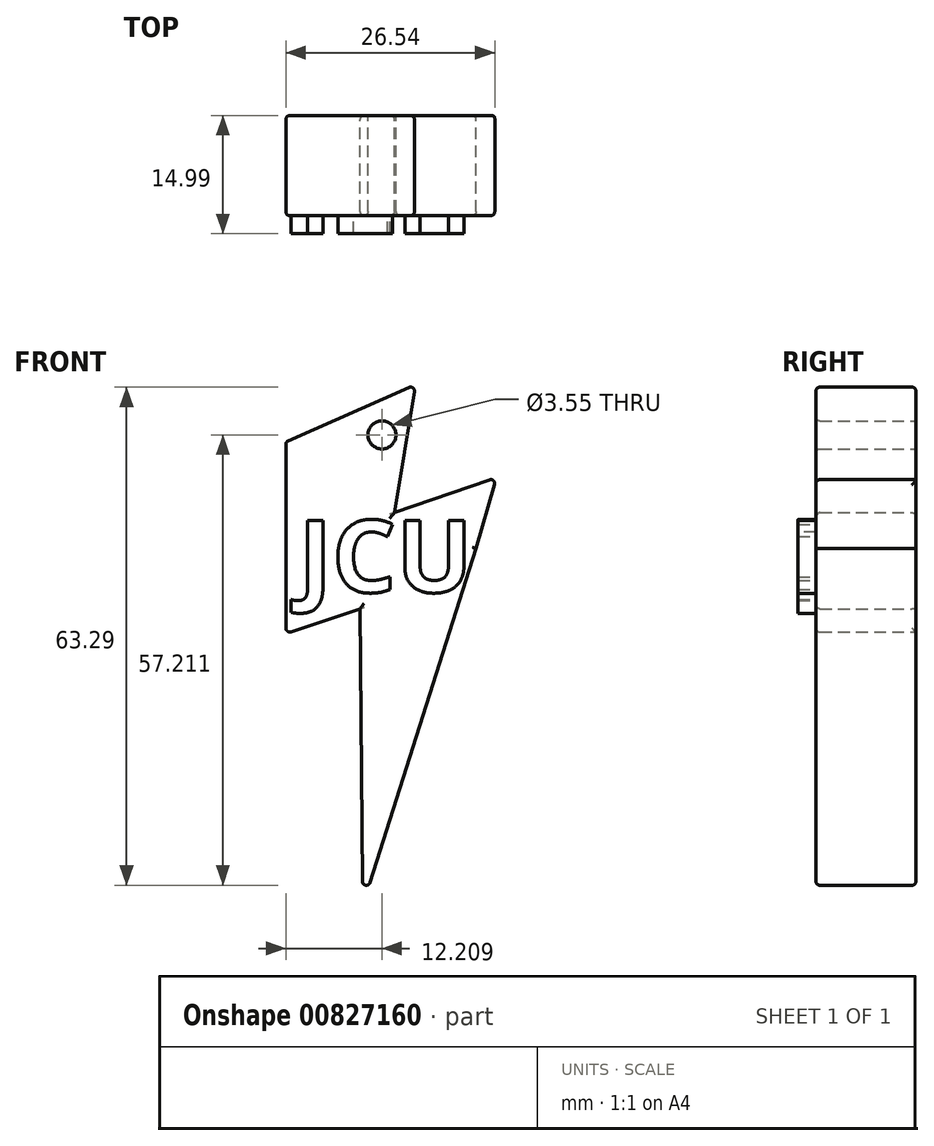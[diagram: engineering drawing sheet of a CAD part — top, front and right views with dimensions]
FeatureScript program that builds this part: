
annotation { "Feature Type Name" : "Feature", "Feature Type Description" : "" }
export const myFeature = defineFeature(function(context is Context, id is Id, definition is map)
    precondition{}
    {
        {
            var Q0;
            Q0=qCreatedBy(makeId("Front.planeOp"),FACE);
            var sketch = newSketch(context, id + "F0", { "sketchPlane" : qUnion([Q0])});
            skLineSegment(sketch, "E0", {"start": v(-13.8, 13.56) * mm, "end": v(-13.8, -10.8) * mm});
            skLineSegment(sketch, "E1", {"start": v(-13.8, -10.8) * mm, "end": v(-4.39, -7.67) * mm});
            skLineSegment(sketch, "E2", {"start": v(-13.8, 13.56) * mm, "end": v(2.7, 20.84) * mm});
            skLineSegment(sketch, "E3", {"start": v(2.7, 20.84) * mm, "end": v(0, 4.56) * mm});
            skLineSegment(sketch, "E4", {"start": v(0, 4.56) * mm, "end": v(12.98, 9.05) * mm});
            skLineSegment(sketch, "E5", {"start": v(12.98, 9.05) * mm, "end": v(10.36, 0) * mm});
            skLineSegment(sketch, "E6", {"start": v(10.36, 0) * mm, "end": v(-4.05, -45.42) * mm});
            skLineSegment(sketch, "E7", {"start": v(-4.05, -45.42) * mm, "end": v(-4.39, -7.67) * mm});
            skSolve(sketch);
        }
        {
            var Q0;
            Q0 = qSketchRegion(id + "F0", true);
            extrude(context, id + "F1", {"entities" : qUnion([Q0]), "depth" : 12.7 * mm, "offsetDistance" : 25.4 * mm});
        }
        {
            var Q0;
            Q0=qCreatedBy(makeId("Front.planeOp"),FACE);
            var sketch = newSketch(context, id + "F2", { "sketchPlane" : qUnion([Q0])});
            skCircle(sketch, "E8", {"center": v(-1.6, 14.43) * mm, "radius": 1.78 * mm});
            skSolve(sketch);
        }
        {
            var Q0;
            Q0 = qSketchRegion(id + "F2", true);
            extrude(context, id + "F3", {"entities" : qUnion([Q0]), "operationType" : NewBodyOperationType.REMOVE, "depth" : 15.24 * mm, "offsetDistance" : 25.4 * mm});
        }
        {
            var Q0;
            Q0=qCreatedBy(makeId("Front.planeOp"),FACE);
            var sketch = newSketch(context, id + "F4", { "sketchPlane" : qUnion([Q0])});
            skText(sketch, "E9", { "text": "JCU", "fontName": "OpenSans-Bold.ttf"});
            const initialGuessF4  = {"E9": [-0.01218, -0.00555, 1, 0, 0.00922]};
            skSetInitialGuess(sketch, initialGuessF4);
            skSolve(sketch);
        }
        {
            var Q0;
            Q0 = qSketchRegion(id + "F4", true);
            extrude(context, id + "F5", {"entities" : qUnion([Q0]), "operationType" : NewBodyOperationType.ADD, "depth" : 15 * mm, "offsetDistance" : 25.4 * mm});
        }
        {
            var Q0;
            Q0=makeQuery(id+"F3.boolean.opBoolean","INTERSECT",EDGE,{"derivedFrom":[makeQuery(id+"F1.opExtrude","CAP_FACE",FACE,{"disambiguationData":[OSD([sQuery(id+"F0.wireOp",EDGE,"E0"),sQuery(id+"F0.wireOp",EDGE,"E1"),sQuery(id+"F0.wireOp",EDGE,"E2"),sQuery(id+"F0.wireOp",EDGE,"E3"),sQuery(id+"F0.wireOp",EDGE,"E4"),sQuery(id+"F0.wireOp",EDGE,"E5"),sQuery(id+"F0.wireOp",EDGE,"E6"),sQuery(id+"F0.wireOp",EDGE,"E7")])],"isStart":false}),makeQuery(id+"F3.opExtrude","SWEPT_FACE",FACE,{"disambiguationData":[OSD([sQuery(id+"F2.wireOp",EDGE,"E8")])]})]});
            var Q1;
            Q1=makeQuery(id+"F3.boolean.opBoolean","COPY",EDGE,{"derivedFrom":makeQuery(id+"F3.opExtrude","CAP_EDGE",EDGE,{"disambiguationData":[OSD([sQuery(id+"F2.wireOp",EDGE,"E8")])],"isStart":true})});
            fillet(context, id + "F6", {"entities" : qUnion([Q0, Q1]), "radius" : .5 * mm, "tangentPropagation" : true, "allowEdgeOverflow" : false});
        }
        {
            var Q0;
            Q0=makeQuery(id+"F1.opExtrude","CAP_EDGE",EDGE,{"disambiguationData":[OSD([sQuery(id+"F0.wireOp",EDGE,"E0")])],"isStart":false});
            var Q1;
            Q1=makeQuery(id+"F1.opExtrude","CAP_EDGE",EDGE,{"disambiguationData":[OSD([sQuery(id+"F0.wireOp",EDGE,"E2")])],"isStart":false});
            var Q2;
            Q2=makeQuery(id+"F1.opExtrude","CAP_EDGE",EDGE,{"disambiguationData":[OSD([sQuery(id+"F0.wireOp",EDGE,"E3")])],"isStart":false});
            var Q3;
            Q3=makeQuery(id+"F1.opExtrude","CAP_EDGE",EDGE,{"disambiguationData":[OSD([sQuery(id+"F0.wireOp",EDGE,"E4")])],"isStart":false});
            var Q4;
            Q4=makeQuery(id+"F1.opExtrude","CAP_EDGE",EDGE,{"disambiguationData":[OSD([sQuery(id+"F0.wireOp",EDGE,"E6")])],"isStart":true});
            var Q5;
            Q5=makeQuery(id+"F1.opExtrude","CAP_EDGE",EDGE,{"disambiguationData":[OSD([sQuery(id+"F0.wireOp",EDGE,"E1")])],"isStart":false});
            var Q6;
            Q6=makeQuery(id+"F1.opExtrude","CAP_EDGE",EDGE,{"disambiguationData":[OSD([sQuery(id+"F0.wireOp",EDGE,"E7")])],"isStart":false});
            var Q7;
            Q7=makeQuery(id+"F1.opExtrude","CAP_EDGE",EDGE,{"disambiguationData":[OSD([sQuery(id+"F0.wireOp",EDGE,"E6")])],"isStart":false});
            var Q8;
            Q8=makeQuery(id+"F1.opExtrude","CAP_EDGE",EDGE,{"disambiguationData":[OSD([sQuery(id+"F0.wireOp",EDGE,"E5")])],"isStart":false});
            var Q9;
            Q9=makeQuery(id+"F1.opExtrude","CAP_EDGE",EDGE,{"disambiguationData":[OSD([sQuery(id+"F0.wireOp",EDGE,"E5")])],"isStart":true});
            var Q10;
            Q10=makeQuery(id+"F1.opExtrude","SWEPT_EDGE",EDGE,{"disambiguationData":[OSD([sQuery(id+"F0.wireOp",EDGE,"E4"),sQuery(id+"F0.wireOp",EDGE,"E5")])]});
            var Q11;
            Q11=makeQuery(id+"F1.opExtrude","SWEPT_EDGE",EDGE,{"disambiguationData":[OSD([sQuery(id+"F0.wireOp",EDGE,"E2"),sQuery(id+"F0.wireOp",EDGE,"E3")])]});
            var Q12;
            Q12=makeQuery(id+"F1.opExtrude","CAP_EDGE",EDGE,{"disambiguationData":[OSD([sQuery(id+"F0.wireOp",EDGE,"E3")])],"isStart":true});
            var Q13;
            Q13=makeQuery(id+"F1.opExtrude","SWEPT_EDGE",EDGE,{"disambiguationData":[OSD([sQuery(id+"F0.wireOp",EDGE,"E0"),sQuery(id+"F0.wireOp",EDGE,"E2")])]});
            var Q14;
            Q14=makeQuery(id+"F1.opExtrude","CAP_EDGE",EDGE,{"disambiguationData":[OSD([sQuery(id+"F0.wireOp",EDGE,"E2")])],"isStart":true});
            var Q15;
            Q15=makeQuery(id+"F1.opExtrude","CAP_EDGE",EDGE,{"disambiguationData":[OSD([sQuery(id+"F0.wireOp",EDGE,"E0")])],"isStart":true});
            var Q16;
            Q16=makeQuery(id+"F1.opExtrude","SWEPT_EDGE",EDGE,{"disambiguationData":[OSD([sQuery(id+"F0.wireOp",EDGE,"E0"),sQuery(id+"F0.wireOp",EDGE,"E1")])]});
            var Q17;
            Q17=makeQuery(id+"F1.opExtrude","CAP_EDGE",EDGE,{"disambiguationData":[OSD([sQuery(id+"F0.wireOp",EDGE,"E7")])],"isStart":true});
            var Q18;
            Q18=makeQuery(id+"F1.opExtrude","SWEPT_EDGE",EDGE,{"disambiguationData":[OSD([sQuery(id+"F0.wireOp",EDGE,"E6"),sQuery(id+"F0.wireOp",EDGE,"E7")])]});
            fillet(context, id + "F7", {"entities" : qUnion([Q0, Q1, Q2, Q3, Q4, Q5, Q6, Q7, Q8, Q9, Q10, Q11, Q12, Q13, Q14, Q15, Q16, Q17, Q18]), "radius" : .5 * mm, "tangentPropagation" : true, "allowEdgeOverflow" : false});
        }
    });
